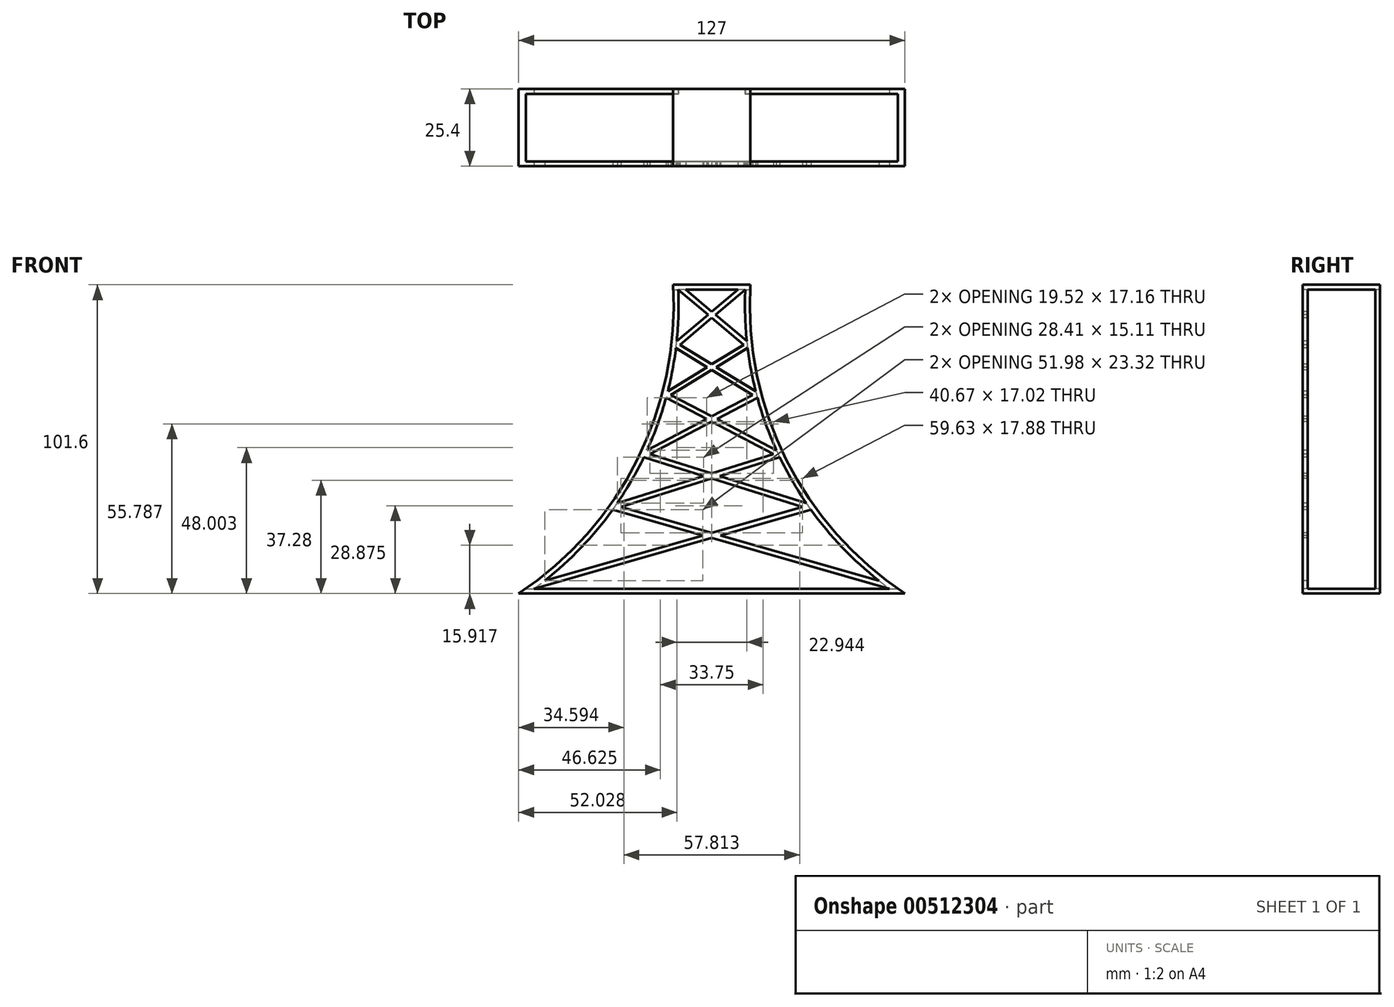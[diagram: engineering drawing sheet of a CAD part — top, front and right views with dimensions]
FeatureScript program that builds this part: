
annotation { "Feature Type Name" : "Feature", "Feature Type Description" : "" }
export const myFeature = defineFeature(function(context is Context, id is Id, definition is map)
    precondition{}
    {
        {
            var Q0;
            Q0=qCreatedBy(makeId("Front.planeOp"),FACE);
            var sketch = newSketch(context, id + "F0", { "sketchPlane" : qUnion([Q0])});
            skLineSegment(sketch, "E0", {"start": v(12.7, 0) * mm, "end": v(76.2, 0) * mm});
            skArc(sketch, "E1", {"start": v(25.4, 101.6) * mm, "mid": v(37.21, 44) * mm, "end": v(76.2, 0) * mm});
            skLineSegment(sketch, "E2", {"start": v(12.7, 101.6) * mm, "end": v(12.7, 0) * mm});
            skPoint(sketch, "E3.orphan", {"position": v(0, 101.6) * mm});
            skPoint(sketch, "E4.end.orphan", {"position": v(25.4, 101.6) * mm});
            skLineSegment(sketch, "E5", {"start": v(25.4, 101.6) * mm, "end": v(12.7, 101.6) * mm});
            skLineSegment(sketch, "E6.MirrorCS", {"start": v(0, 101.6) * mm, "end": v(12.7, 101.6) * mm});
            skArc(sketch, "E7.MirrorCS", {"start": v(0, 101.6) * mm, "mid": v(-11.81, 44) * mm, "end": v(-50.8, 0) * mm});
            skLineSegment(sketch, "E8.MirrorCS", {"start": v(12.7, 0) * mm, "end": v(-50.8, 0) * mm});
            skSolve(sketch);
        }
        {
            var Q0;
            Q0=makeQuery(id+"F0.imprint","IMPRINT",FACE,{"disambiguationData":[TD([[makeQuery(id+"F0.imprint","IMPRINT",EDGE,{"derivedFrom":sQuery(id+"F0.wireOp",EDGE,"E0")}),1.0]])]});
            var Q1;
            Q1=makeQuery(id+"F0.imprint","IMPRINT",FACE,{"disambiguationData":[TD([[makeQuery(id+"F0.imprint","IMPRINT",EDGE,{"derivedFrom":sQuery(id+"F0.wireOp",EDGE,"E2")}),-1.0]])]});
            extrude(context, id + "F1", {"entities" : qUnion([Q0, Q1]), "depth" : 25.4 * mm});
        }
        {
            var Q0;
            Q0=makeQuery(id+"F1.opExtrude","CAP_FACE",FACE,{"disambiguationData":[OSD([sQuery(id+"F0.wireOp",EDGE,"E0"),sQuery(id+"F0.wireOp",EDGE,"E1"),sQuery(id+"F0.wireOp",EDGE,"E5"),sQuery(id+"F0.wireOp",EDGE,"E6.MirrorCS"),sQuery(id+"F0.wireOp",EDGE,"E7.MirrorCS"),sQuery(id+"F0.wireOp",EDGE,"E8.MirrorCS")])],"isStart":false});
            var sketch = newSketch(context, id + "F2", { "sketchPlane" : qUnion([Q0])});
            skArc(sketch, "E9.0", {"start": v(23.73, 100.01) * mm, "mid": v(35.04, 44.83) * mm, "end": v(71.13, 1.59) * mm});
            skLineSegment(sketch, "E9.1", {"start": v(23.73, 100.01) * mm, "end": v(1.67, 100.01) * mm});
            skArc(sketch, "E9.2", {"start": v(1.67, 100.01) * mm, "mid": v(-9.64, 44.83) * mm, "end": v(-45.73, 1.59) * mm});
            skLineSegment(sketch, "E9.3", {"start": v(-45.73, 1.59) * mm, "end": v(71.13, 1.59) * mm});
            skSolve(sketch);
        }
        {
            var Q0;
            Q0=makeQuery(id+"F2.imprint","IMPRINT",FACE,{"disambiguationData":[TD([[makeQuery(id+"F2.imprint","IMPRINT",EDGE,{"derivedFrom":sQuery(id+"F2.wireOp",EDGE,"E9.0")}),-1.0]])]});
            extrude(context, id + "F3", {"entities" : qUnion([Q0]), "operationType" : NewBodyOperationType.REMOVE, "endBound" : BoundingType.THROUGH_ALL, "oppositeDirection" : true, "depth" : 25.4 * mm});
        }
        {
            var Q0;
            Q0=qCreatedBy(makeId("Right.planeOp"),FACE);
            cPlane(context, id + "F4", {"entities" : qUnion([Q0]), "cplaneType" : CPlaneType.OFFSET, "offset" : 83.82 * mm, "width" : 152.4 * mm, "height" : 152.4 * mm});
        }
        {
            var Q0;
            Q0=qCreatedBy(id+"F4.planeOp",FACE);
            var sketch = newSketch(context, id + "F5", { "sketchPlane" : qUnion([Q0])});
            skLineSegment(sketch, "E10.0.0", {"start": v(0, 0) * mm, "end": v(0, 101.6) * mm});
            skLineSegment(sketch, "E10.0.1", {"start": v(0, 101.6) * mm, "end": v(-25.4, 101.6) * mm});
            skLineSegment(sketch, "E10.0.2", {"start": v(-25.4, 101.6) * mm, "end": v(-25.4, 0) * mm});
            skLineSegment(sketch, "E10.0.3", {"start": v(-25.4, 0) * mm, "end": v(0, 0) * mm});
            skLineSegment(sketch, "E11.0", {"start": v(-1.59, 1.59) * mm, "end": v(-1.59, 100.01) * mm});
            skLineSegment(sketch, "E11.1", {"start": v(-23.81, 1.59) * mm, "end": v(-1.59, 1.59) * mm});
            skLineSegment(sketch, "E11.2", {"start": v(-23.81, 100.01) * mm, "end": v(-23.81, 1.59) * mm});
            skLineSegment(sketch, "E11.3", {"start": v(-1.59, 100.01) * mm, "end": v(-23.81, 100.01) * mm});
            skSolve(sketch);
        }
        {
            var Q0;
            Q0=makeQuery(id+"F5.imprint","IMPRINT",FACE,{"disambiguationData":[TD([[makeQuery(id+"F5.imprint","IMPRINT",EDGE,{"derivedFrom":sQuery(id+"F5.wireOp",EDGE,"E11.0")}),1.0]])]});
            extrude(context, id + "F6", {"entities" : qUnion([Q0]), "operationType" : NewBodyOperationType.REMOVE, "endBound" : BoundingType.THROUGH_ALL, "oppositeDirection" : true, "depth" : 25.4 * mm});
        }
        {
            var Q0;
            Q0=makeQuery(id+"F1.opExtrude","CAP_FACE",FACE,{"disambiguationData":[OSD([sQuery(id+"F0.wireOp",EDGE,"E0"),sQuery(id+"F0.wireOp",EDGE,"E1"),sQuery(id+"F0.wireOp",EDGE,"E5"),sQuery(id+"F0.wireOp",EDGE,"E6.MirrorCS"),sQuery(id+"F0.wireOp",EDGE,"E7.MirrorCS"),sQuery(id+"F0.wireOp",EDGE,"E8.MirrorCS")])],"isStart":false});
            var sketch = newSketch(context, id + "F7", { "sketchPlane" : qUnion([Q0])});
            skLineSegment(sketch, "E12", {"start": v(23.73, 100.01) * mm, "end": v(13.93, 91.75) * mm});
            skLineSegment(sketch, "E13", {"start": v(0.92, 80.77) * mm, "end": v(11.18, 74.49) * mm});
            skLineSegment(sketch, "E14", {"start": v(27.73, 64.37) * mm, "end": v(14.41, 57.4) * mm});
            skLineSegment(sketch, "E15", {"start": v(-9.64, 44.83) * mm, "end": v(10.03, 38.65) * mm});
            skLineSegment(sketch, "E16", {"start": v(45.29, 27.58) * mm, "end": v(15.61, 19.1) * mm});
            skLineSegment(sketch, "E17", {"start": v(-45.73, 1.59) * mm, "end": v(-45.06, 2.38) * mm});
            skLineSegment(sketch, "E18", {"start": v(12.7, 100.01) * mm, "end": v(12.7, 1.59) * mm});
            skLineSegment(sketch, "E19.MirrorCS", {"start": v(1.67, 100.01) * mm, "end": v(11.47, 91.75) * mm});
            skLineSegment(sketch, "E20.MirrorCS", {"start": v(24.48, 80.77) * mm, "end": v(-2.33, 64.37) * mm});
            skLineSegment(sketch, "E21.MirrorCS", {"start": v(-2.33, 64.37) * mm, "end": v(10.99, 57.4) * mm});
            skLineSegment(sketch, "E22.MirrorCS", {"start": v(35.04, 44.83) * mm, "end": v(15.37, 38.65) * mm});
            skLineSegment(sketch, "E23.MirrorCS", {"start": v(-19.89, 27.58) * mm, "end": v(9.79, 19.1) * mm});
            skLineSegment(sketch, "E24.0", {"start": v(21.27, 100.01) * mm, "end": v(12.7, 92.78) * mm});
            skArc(sketch, "E25.0.0", {"start": v(76.2, 0) * mm, "mid": v(37.21, 44) * mm, "end": v(25.4, 101.6) * mm});
            skLineSegment(sketch, "E25.0.1", {"start": v(25.4, 101.6) * mm, "end": v(0, 101.6) * mm});
            skArc(sketch, "E25.0.2", {"start": v(0, 101.6) * mm, "mid": v(-11.81, 44) * mm, "end": v(-50.8, 0) * mm});
            skLineSegment(sketch, "E25.0.3", {"start": v(-50.8, 0) * mm, "end": v(76.2, 0) * mm});
            skLineSegment(sketch, "E26.0", {"start": v(23.73, 100.01) * mm, "end": v(1.67, 100.01) * mm});
            skArc(sketch, "E27.0", {"start": v(1.67, 100.01) * mm, "mid": v(-9.64, 44.83) * mm, "end": v(-45.73, 1.59) * mm});
            skArc(sketch, "E28.0", {"start": v(23.73, 100.01) * mm, "mid": v(35.04, 44.83) * mm, "end": v(71.13, 1.59) * mm});
            skLineSegment(sketch, "E29.0", {"start": v(23.2, 81.84) * mm, "end": v(12.7, 75.42) * mm});
            skLineSegment(sketch, "E30.0", {"start": v(27.3, 65.94) * mm, "end": v(12.7, 58.3) * mm});
            skLineSegment(sketch, "E31.0", {"start": v(34.56, 46.36) * mm, "end": v(12.7, 39.5) * mm});
            skLineSegment(sketch, "E32.0", {"start": v(44.31, 28.96) * mm, "end": v(12.7, 19.93) * mm});
            skLineSegment(sketch, "E33.MirrorCS", {"start": v(4.13, 100.01) * mm, "end": v(12.7, 92.78) * mm});
            skLineSegment(sketch, "E34.MirrorCS", {"start": v(2.2, 81.84) * mm, "end": v(12.7, 75.42) * mm});
            skLineSegment(sketch, "E35.MirrorCS", {"start": v(-1.9, 65.94) * mm, "end": v(12.7, 58.3) * mm});
            skLineSegment(sketch, "E36.MirrorCS", {"start": v(-9.16, 46.36) * mm, "end": v(12.7, 39.5) * mm});
            skLineSegment(sketch, "E37.MirrorCS", {"start": v(-18.91, 28.96) * mm, "end": v(12.7, 19.93) * mm});
            skLineSegment(sketch, "E38.trimOffspring", {"start": v(15.61, 19.1) * mm, "end": v(67.6, 4.26) * mm});
            skLineSegment(sketch, "E39.trimOffspring", {"start": v(12.7, 18.27) * mm, "end": v(71.13, 1.59) * mm});
            skLineSegment(sketch, "E40.trimOffspring", {"start": v(9.79, 19.1) * mm, "end": v(-42.2, 4.26) * mm});
            skLineSegment(sketch, "E41.trimOffspring", {"start": v(12.7, 18.27) * mm, "end": v(-45.73, 1.59) * mm});
            skLineSegment(sketch, "E42.trimOffspring", {"start": v(10.03, 38.65) * mm, "end": v(-20.37, 29.1) * mm});
            skLineSegment(sketch, "E43.trimOffspring", {"start": v(15.37, 38.65) * mm, "end": v(45.77, 29.1) * mm});
            skLineSegment(sketch, "E44.trimOffspring", {"start": v(12.7, 37.81) * mm, "end": v(45.29, 27.58) * mm});
            skLineSegment(sketch, "E45.trimOffspring", {"start": v(12.7, 37.81) * mm, "end": v(-19.89, 27.58) * mm});
            skLineSegment(sketch, "E46.trimOffspring", {"start": v(10.99, 57.4) * mm, "end": v(-8.53, 47.2) * mm});
            skLineSegment(sketch, "E47.trimOffspring", {"start": v(12.7, 56.51) * mm, "end": v(-9.64, 44.83) * mm});
            skLineSegment(sketch, "E48.trimOffspring", {"start": v(14.41, 57.4) * mm, "end": v(33.93, 47.2) * mm});
            skLineSegment(sketch, "E49.trimOffspring", {"start": v(12.7, 56.51) * mm, "end": v(35.04, 44.83) * mm});
            skLineSegment(sketch, "E50.trimOffspring", {"start": v(14.22, 74.49) * mm, "end": v(27.14, 66.59) * mm});
            skLineSegment(sketch, "E51.trimOffspring", {"start": v(11.18, 74.49) * mm, "end": v(-1.74, 66.59) * mm});
            skLineSegment(sketch, "E52.trimOffspring", {"start": v(12.7, 73.56) * mm, "end": v(27.73, 64.37) * mm});
            skLineSegment(sketch, "E53.trimOffspring", {"start": v(11.47, 91.75) * mm, "end": v(1.18, 83.06) * mm});
            skLineSegment(sketch, "E54.trimOffspring", {"start": v(13.93, 91.75) * mm, "end": v(24.22, 83.06) * mm});
            skPoint(sketch, "E55.MirrorCS.start.orphan", {"position": v(4.13, 100.01) * mm});
            skLineSegment(sketch, "E56.trimOffspring", {"start": v(12.7, 90.7) * mm, "end": v(2.2, 81.84) * mm});
            skLineSegment(sketch, "E57.trimOffspring", {"start": v(12.7, 90.7) * mm, "end": v(23.2, 81.84) * mm});
            skPoint(sketch, "E58.MirrorCS.start.orphan", {"position": v(1.67, 100.01) * mm});
            skPoint(sketch, "E59.orphan", {"position": v(24.48, 80.77) * mm});
            skPoint(sketch, "E60.orphan", {"position": v(24.28, 82.5) * mm});
            skPoint(sketch, "E61.orphan", {"position": v(1.12, 82.5) * mm});
            skPoint(sketch, "E62.orphan", {"position": v(1.18, 83.06) * mm});
            skSolve(sketch);
        }
        {
            var Q0;
            {var subQ7=sQuery(id+"F7.wireOp",EDGE,"E12");Q0=makeQuery(id+"F7.imprint","IMPRINT",FACE,{"disambiguationData":[TD([[makeQuery(id+"F7.imprint","IMPRINT",EDGE,{"derivedFrom":subQ7}),-1.0]])]});}
            var Q1;
            {var subQ8=sQuery(id+"F7.wireOp",EDGE,"E13");Q1=makeQuery(id+"F7.imprint","IMPRINT",FACE,{"disambiguationData":[TD([[makeQuery(id+"F7.imprint","IMPRINT",EDGE,{"derivedFrom":subQ8}),1.0]])]});}
            var Q2;
            {var subQ0=sQuery(id+"F7.wireOp",EDGE,"E50.trimOffspring");Q2=makeQuery(id+"F7.imprint","IMPRINT",FACE,{"disambiguationData":[TD([[makeQuery(id+"F7.imprint","IMPRINT",EDGE,{"derivedFrom":subQ0}),-1.0]])]});}
            var Q3;
            {var subQ4=sQuery(id+"F7.wireOp",EDGE,"E21.MirrorCS");Q3=makeQuery(id+"F7.imprint","IMPRINT",FACE,{"disambiguationData":[TD([[makeQuery(id+"F7.imprint","IMPRINT",EDGE,{"derivedFrom":subQ4}),1.0]])]});}
            var Q4;
            {var subQ11=sQuery(id+"F7.wireOp",EDGE,"E14");Q4=makeQuery(id+"F7.imprint","IMPRINT",FACE,{"disambiguationData":[TD([[makeQuery(id+"F7.imprint","IMPRINT",EDGE,{"derivedFrom":subQ11}),-1.0]])]});}
            var Q5;
            {var subQ13=sQuery(id+"F7.wireOp",EDGE,"E15");Q5=makeQuery(id+"F7.imprint","IMPRINT",FACE,{"disambiguationData":[TD([[makeQuery(id+"F7.imprint","IMPRINT",EDGE,{"derivedFrom":subQ13}),1.0]])]});}
            var Q6;
            {var subQ10=sQuery(id+"F7.wireOp",EDGE,"E22.MirrorCS");Q6=makeQuery(id+"F7.imprint","IMPRINT",FACE,{"disambiguationData":[TD([[makeQuery(id+"F7.imprint","IMPRINT",EDGE,{"derivedFrom":subQ10}),-1.0]])]});}
            var Q7;
            {var subQ8=sQuery(id+"F7.wireOp",EDGE,"E16");Q7=makeQuery(id+"F7.imprint","IMPRINT",FACE,{"disambiguationData":[TD([[makeQuery(id+"F7.imprint","IMPRINT",EDGE,{"derivedFrom":subQ8}),-1.0]])]});}
            var Q8;
            {var subQ3=sQuery(id+"F7.wireOp",EDGE,"E23.MirrorCS");Q8=makeQuery(id+"F7.imprint","IMPRINT",FACE,{"disambiguationData":[TD([[makeQuery(id+"F7.imprint","IMPRINT",EDGE,{"derivedFrom":subQ3}),1.0]])]});}
            var Q9;
            {var subQ1=sQuery(id+"F7.wireOp",EDGE,"E27.0");var subQ3=sQuery(id+"F7.wireOp",EDGE,"E37.MirrorCS");var subQ4=makeQuery(id+"F7.imprint","INTERSECT",VERTEX,{"derivedFrom":[subQ1,subQ3]});Q9=makeQuery(id+"F7.imprint","IMPRINT",FACE,{"disambiguationData":[TD([[makeQuery(id+"F7.imprint","IMPRINT",EDGE,{"disambiguationData":[TD([[subQ4,-1.0]])],"derivedFrom":subQ3}),-1.0]])]});}
            var Q10;
            {var subQ1=sQuery(id+"F7.wireOp",EDGE,"E28.0");var subQ3=sQuery(id+"F7.wireOp",EDGE,"E31.0");var subQ4=makeQuery(id+"F7.imprint","INTERSECT",VERTEX,{"derivedFrom":[subQ1,subQ3]});Q10=makeQuery(id+"F7.imprint","IMPRINT",FACE,{"disambiguationData":[TD([[makeQuery(id+"F7.imprint","IMPRINT",EDGE,{"disambiguationData":[TD([[subQ4,-1.0]])],"derivedFrom":subQ3}),1.0]])]});}
            var Q11;
            {var subQ1=sQuery(id+"F7.wireOp",EDGE,"E28.0");var subQ3=sQuery(id+"F7.wireOp",EDGE,"E32.0");var subQ4=makeQuery(id+"F7.imprint","INTERSECT",VERTEX,{"derivedFrom":[subQ1,subQ3]});Q11=makeQuery(id+"F7.imprint","IMPRINT",FACE,{"disambiguationData":[TD([[makeQuery(id+"F7.imprint","IMPRINT",EDGE,{"disambiguationData":[TD([[subQ4,-1.0]])],"derivedFrom":subQ3}),1.0]])]});}
            var Q12;
            {var subQ1=sQuery(id+"F7.wireOp",EDGE,"E27.0");var subQ3=sQuery(id+"F7.wireOp",EDGE,"E36.MirrorCS");var subQ4=makeQuery(id+"F7.imprint","INTERSECT",VERTEX,{"derivedFrom":[subQ1,subQ3]});Q12=makeQuery(id+"F7.imprint","IMPRINT",FACE,{"disambiguationData":[TD([[makeQuery(id+"F7.imprint","IMPRINT",EDGE,{"disambiguationData":[TD([[subQ4,-1.0]])],"derivedFrom":subQ3}),-1.0]])]});}
            var Q13;
            {var subQ1=sQuery(id+"F7.wireOp",EDGE,"E28.0");var subQ3=sQuery(id+"F7.wireOp",EDGE,"E30.0");var subQ4=makeQuery(id+"F7.imprint","INTERSECT",VERTEX,{"derivedFrom":[subQ1,subQ3]});Q13=makeQuery(id+"F7.imprint","IMPRINT",FACE,{"disambiguationData":[TD([[makeQuery(id+"F7.imprint","IMPRINT",EDGE,{"disambiguationData":[TD([[subQ4,-1.0]])],"derivedFrom":subQ3}),1.0]])]});}
            var Q14;
            {var subQ0=sQuery(id+"F7.wireOp",EDGE,"E27.0");var subQ3=sQuery(id+"F7.wireOp",EDGE,"E35.MirrorCS");var subQ5=makeQuery(id+"F7.imprint","INTERSECT",VERTEX,{"derivedFrom":[subQ0,subQ3]});Q14=makeQuery(id+"F7.imprint","IMPRINT",FACE,{"disambiguationData":[TD([[makeQuery(id+"F7.imprint","IMPRINT",EDGE,{"disambiguationData":[TD([[subQ5,-1.0]])],"derivedFrom":subQ3}),-1.0]])]});}
            extrude(context, id + "F8", {"entities" : qUnion([Q0, Q1, Q2, Q3, Q4, Q5, Q6, Q7, Q8, Q9, Q10, Q11, Q12, Q13, Q14]), "operationType" : NewBodyOperationType.ADD, "oppositeDirection" : true, "depth" : 1.59 * mm});
        }
    });
